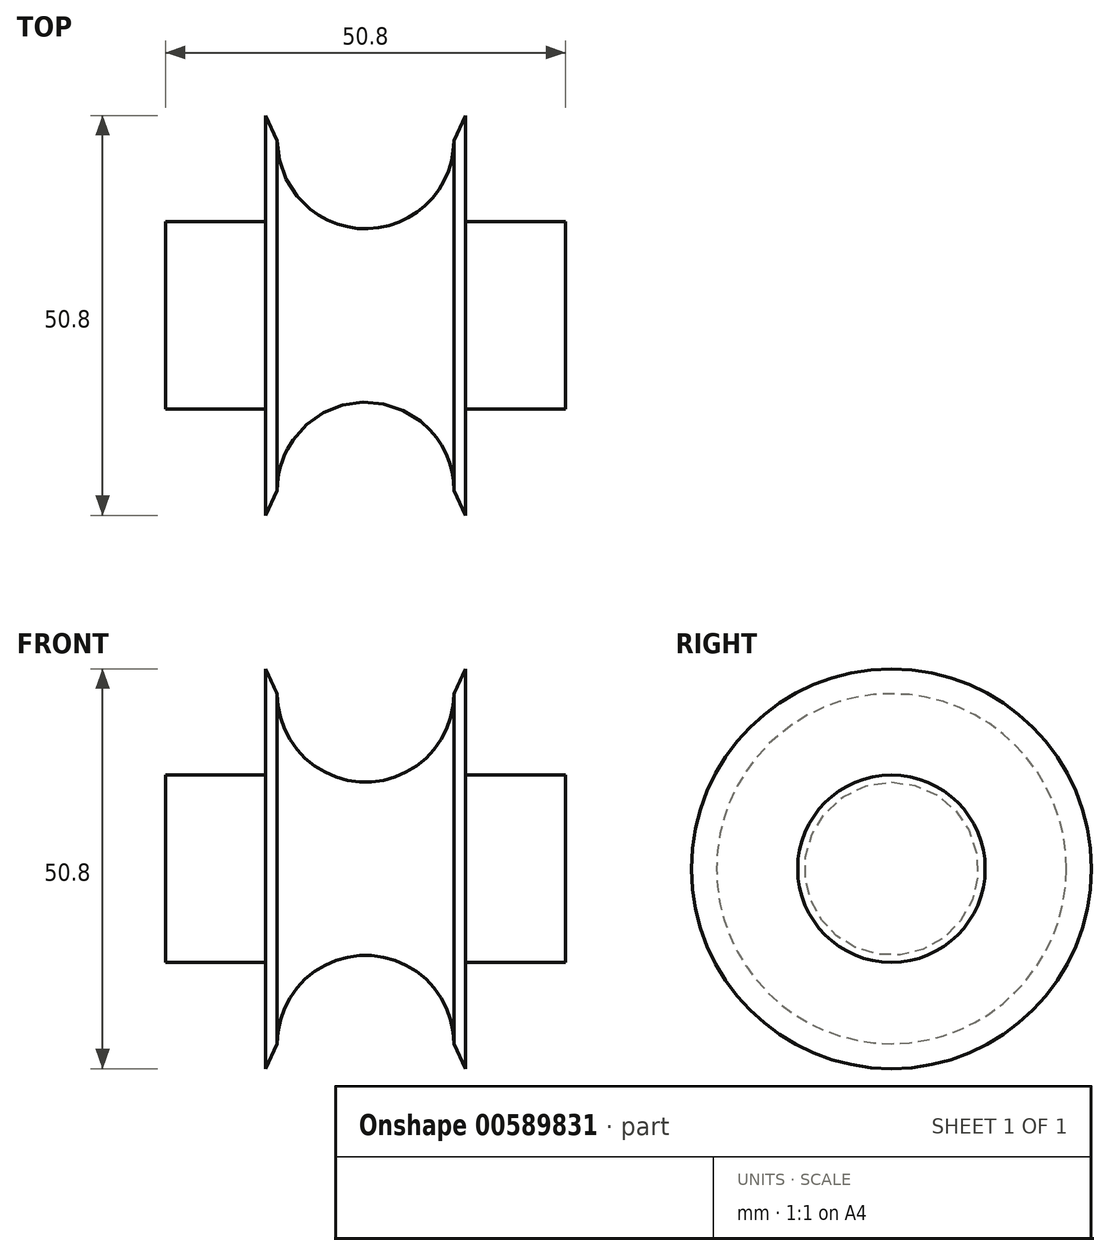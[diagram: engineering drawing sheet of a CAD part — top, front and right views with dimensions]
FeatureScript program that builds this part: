
annotation { "Feature Type Name" : "Feature", "Feature Type Description" : "" }
export const myFeature = defineFeature(function(context is Context, id is Id, definition is map)
    precondition{}
    {
        {
            var Q0;
            Q0=qCreatedBy(makeId("Front.planeOp"),FACE);
            var sketch = newSketch(context, id + "F0", { "sketchPlane" : qUnion([Q0])});
            skLineSegment(sketch, "E0", {"start": v(-25.4, 0) * mm, "end": v(-25.4, 25.4) * mm});
            skLineSegment(sketch, "E1", {"start": v(0, 0) * mm, "end": v(0, 25.4) * mm});
            skLineSegment(sketch, "E2", {"start": v(0, 25.4) * mm, "end": v(-1.48, 22.23) * mm});
            skLineSegment(sketch, "E3", {"start": v(-25.4, 25.4) * mm, "end": v(-23.92, 22.23) * mm});
            skArc(sketch, "E4", {"start": v(-23.92, 22.23) * mm, "mid": v(-12.7, 11) * mm, "end": v(-1.48, 22.23) * mm});
            skLineSegment(sketch, "E5", {"start": v(-1.48, 22.23) * mm, "end": v(-1.48, 33.76) * mm, "construction": true});
            skLineSegment(sketch, "E6", {"start": v(-23.92, 22.23) * mm, "end": v(-23.92, 33.33) * mm, "construction": true});
            skLineSegment(sketch, "E7", {"start": v(-25.4, 11.9) * mm, "end": v(-38.1, 11.9) * mm});
            skLineSegment(sketch, "E8", {"start": v(-38.1, 11.9) * mm, "end": v(-38.1, 0) * mm});
            skLineSegment(sketch, "E9", {"start": v(0, 11.9) * mm, "end": v(12.7, 11.9) * mm});
            skLineSegment(sketch, "E10", {"start": v(12.7, 11.9) * mm, "end": v(12.7, 0) * mm});
            skLineSegment(sketch, "E11", {"start": v(-44.29, 0) * mm, "end": v(20.59, 0) * mm});
            skSolve(sketch);
        }
        {
            var Q0;
            {var subQ3=sQuery(id+"F0.wireOp",EDGE,"E7");Q0=makeQuery(id+"F0.imprint","IMPRINT",FACE,{"disambiguationData":[TD([[makeQuery(id+"F0.imprint","IMPRINT",EDGE,{"derivedFrom":subQ3}),1.0]])]});}
            var Q1;
            {var subQ0=sQuery(id+"F0.wireOp",EDGE,"E2");Q1=makeQuery(id+"F0.imprint","IMPRINT",FACE,{"disambiguationData":[TD([[makeQuery(id+"F0.imprint","IMPRINT",EDGE,{"derivedFrom":subQ0}),1.0]])]});}
            var Q2;
            {var subQ3=sQuery(id+"F0.wireOp",EDGE,"E9");Q2=makeQuery(id+"F0.imprint","IMPRINT",FACE,{"disambiguationData":[TD([[makeQuery(id+"F0.imprint","IMPRINT",EDGE,{"derivedFrom":subQ3}),-1.0]])]});}
            var Q3;
            Q3=sQuery(id+"F0.wireOp",EDGE,"E11");
            revolve(context, id + "F1", {"entities" : qUnion([Q0, Q1, Q2]), "axis" : qUnion([Q3]), "revolveType" : RevolveType.FULL});
        }
    });
